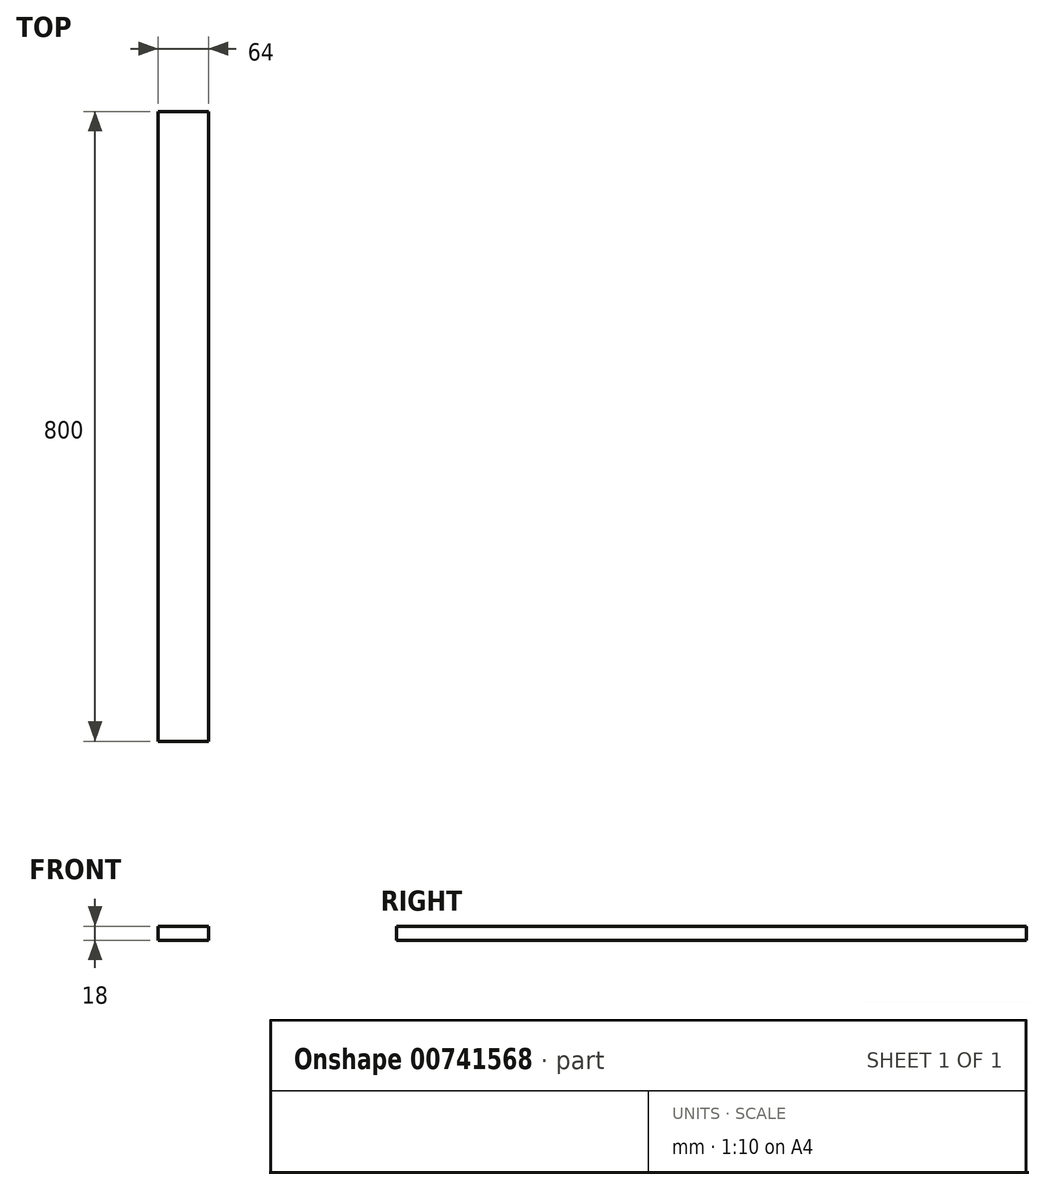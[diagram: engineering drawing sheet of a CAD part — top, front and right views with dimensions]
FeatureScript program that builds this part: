
annotation { "Feature Type Name" : "Feature", "Feature Type Description" : "" }
export const myFeature = defineFeature(function(context is Context, id is Id, definition is map)
    precondition{}
    {
        {
            var Q0;
            Q0=qCreatedBy(makeId("Top.planeOp"),FACE);
            var sketch = newSketch(context, id + "F0", { "sketchPlane" : qUnion([Q0])});
            skLineSegment(sketch, "E0.bottom", {"start": v(-32, -400) * mm, "end": v(32, -400) * mm});
            skLineSegment(sketch, "E0.top", {"start": v(-32, 400) * mm, "end": v(32, 400) * mm});
            skLineSegment(sketch, "E0.left", {"start": v(-32, -400) * mm, "end": v(-32, 400) * mm});
            skLineSegment(sketch, "E0.right", {"start": v(32, -400) * mm, "end": v(32, 400) * mm});
            skPoint(sketch, "E0.middle", {"position": v(0, 0) * mm});
            skSolve(sketch);
        }
        {
            var Q0;
            Q0=qSketchRegion(id+"F0",true);
            extrude(context, id + "F1", {"entities" : qUnion([Q0]), "depth" : 18 * mm, "offsetDistance" : 25 * mm});
        }
    });
